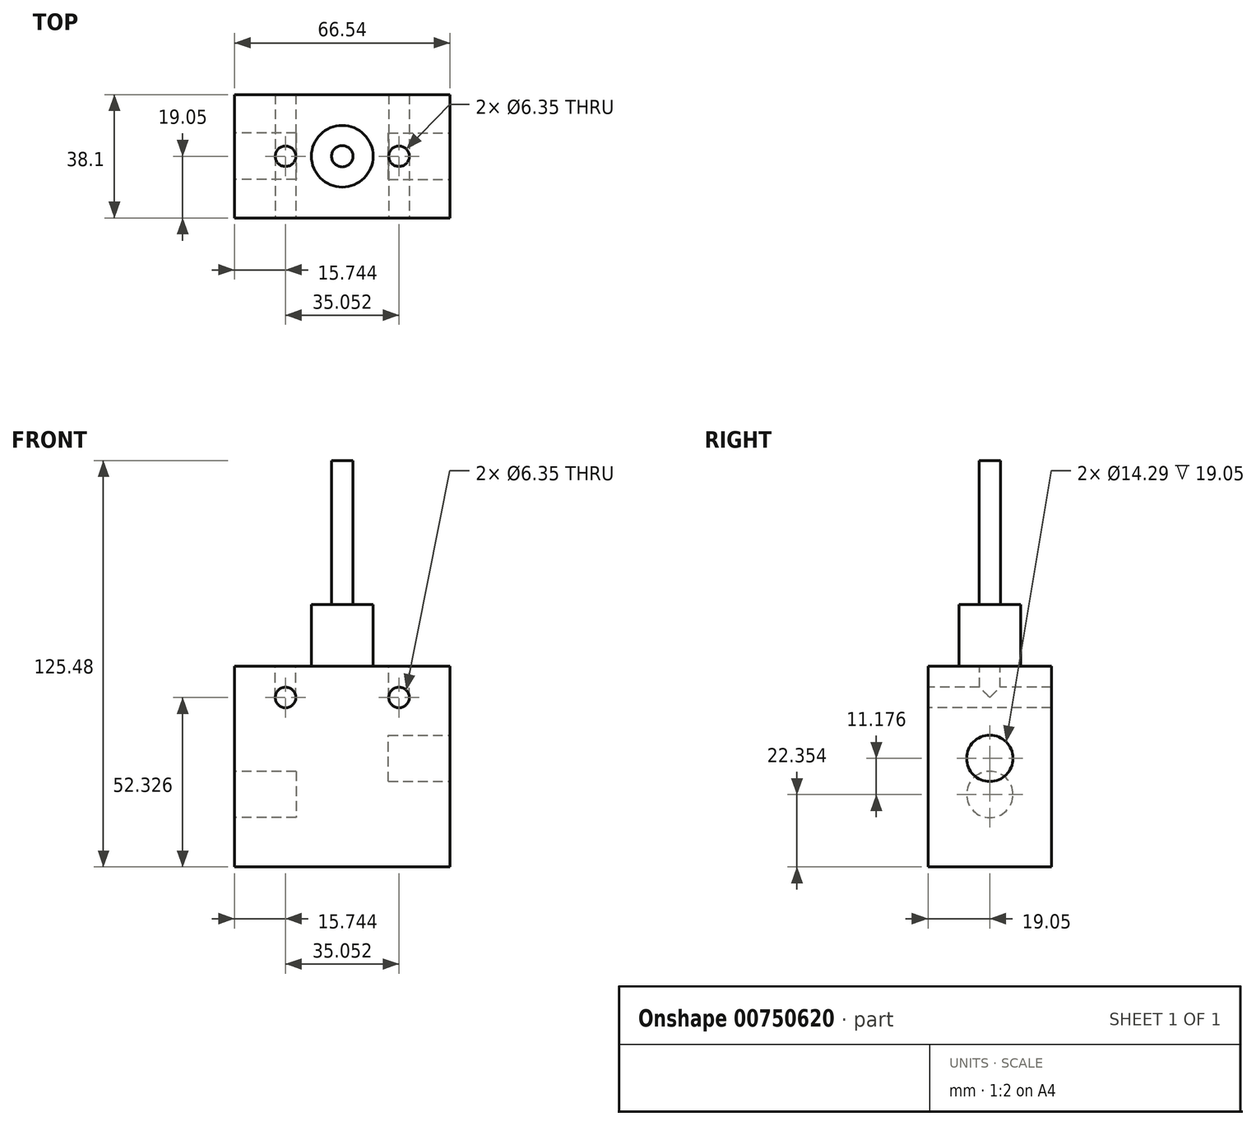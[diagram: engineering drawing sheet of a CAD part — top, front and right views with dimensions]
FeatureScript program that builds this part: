
annotation { "Feature Type Name" : "Feature", "Feature Type Description" : "" }
export const myFeature = defineFeature(function(context is Context, id is Id, definition is map)
    precondition{}
    {
        {
            var Q0;
            Q0=qCreatedBy(makeId("Front.planeOp"),FACE);
            var sketch = newSketch(context, id + "F0", { "sketchPlane" : qUnion([Q0])});
            skLineSegment(sketch, "E0.bottom", {"start": v(-33.27, 30.99) * mm, "end": v(33.27, 30.99) * mm});
            skLineSegment(sketch, "E0.top", {"start": v(-33.27, -30.99) * mm, "end": v(33.27, -30.99) * mm});
            skLineSegment(sketch, "E0.left", {"start": v(-33.27, 30.99) * mm, "end": v(-33.27, -30.99) * mm});
            skLineSegment(sketch, "E0.right", {"start": v(33.27, 30.99) * mm, "end": v(33.27, -30.99) * mm});
            skSolve(sketch);
        }
        {
            var Q0;
            Q0=makeQuery(id+"F0.imprint","IMPRINT",FACE,{"disambiguationData":[TD([[makeQuery(id+"F0.imprint","IMPRINT",EDGE,{"derivedFrom":sQuery(id+"F0.wireOp",EDGE,"E0.bottom")}),-1.0]])]});
            extrude(context, id + "F1", {"entities" : qUnion([Q0]), "endBound" : BoundingType.SYMMETRIC, "depth" : 38.1 * mm, "offsetDistance" : 25.4 * mm});
        }
        {
            var Q0;
            Q0=makeQuery(id+"F1.opExtrude","SWEPT_FACE",FACE,{"disambiguationData":[OSD([sQuery(id+"F0.wireOp",EDGE,"E0.bottom")])]});
            var sketch = newSketch(context, id + "F2", { "sketchPlane" : qUnion([Q0])});
            skCircle(sketch, "E1", {"center": v(0, 0) * mm, "radius": 9.53 * mm});
            skCircle(sketch, "E2", {"center": v(0, 0) * mm, "radius": 3.3 * mm});
            skCircle(sketch, "E3", {"center": v(-17.53, 0) * mm, "radius": 3.18 * mm});
            skCircle(sketch, "E4", {"center": v(17.53, 0) * mm, "radius": 3.18 * mm});
            skSolve(sketch);
        }
        {
            var Q0;
            Q0=makeQuery(id+"F2.imprint","IMPRINT",FACE,{"disambiguationData":[TD([[makeQuery(id+"F2.imprint","IMPRINT",EDGE,{"derivedFrom":sQuery(id+"F2.wireOp",EDGE,"E1")}),1.0]])]});
            extrude(context, id + "F3", {"entities" : qUnion([Q0]), "operationType" : NewBodyOperationType.ADD, "depth" : 19.05 * mm, "offsetDistance" : 25.4 * mm});
        }
        {
            var Q0;
            Q0=makeQuery(id+"F3.boolean.opBoolean","SPLIT",FACE,{"disambiguationData":[TD([makeQuery(id+"F3.opExtrude","SWEPT_FACE",FACE,{"disambiguationData":[OSD([sQuery(id+"F2.wireOp",EDGE,"E2")])]})])],"derivedFrom":makeQuery(id+"F1.opExtrude","SWEPT_FACE",FACE,{"disambiguationData":[OSD([sQuery(id+"F0.wireOp",EDGE,"E0.bottom")])]})});
            extrude(context, id + "F4", {"entities" : qUnion([Q0]), "operationType" : NewBodyOperationType.ADD, "depth" : 63.5 * mm, "offsetDistance" : 25.4 * mm});
        }
        {
            var Q0;
            Q0=makeQuery(id+"F2.imprint","IMPRINT",FACE,{"disambiguationData":[TD([[makeQuery(id+"F2.imprint","IMPRINT",EDGE,{"derivedFrom":sQuery(id+"F2.wireOp",EDGE,"E3")}),1.0]])]});
            var Q1;
            Q1=makeQuery(id+"F2.imprint","IMPRINT",FACE,{"disambiguationData":[TD([[makeQuery(id+"F2.imprint","IMPRINT",EDGE,{"derivedFrom":sQuery(id+"F2.wireOp",EDGE,"E4")}),1.0]])]});
            extrude(context, id + "F5", {"entities" : qUnion([Q0, Q1]), "operationType" : NewBodyOperationType.REMOVE, "oppositeDirection" : true, "depth" : 9.65 * mm, "offsetDistance" : 25.4 * mm});
        }
        {
            var Q0;
            Q0=makeQuery(id+"F1.opExtrude","CAP_FACE",FACE,{"disambiguationData":[OSD([sQuery(id+"F0.wireOp",EDGE,"E0.bottom"),sQuery(id+"F0.wireOp",EDGE,"E0.top"),sQuery(id+"F0.wireOp",EDGE,"E0.left"),sQuery(id+"F0.wireOp",EDGE,"E0.right")])],"isStart":false});
            var sketch = newSketch(context, id + "F6", { "sketchPlane" : qUnion([Q0])});
            skCircle(sketch, "E5", {"center": v(-17.53, 21.34) * mm, "radius": 3.18 * mm});
            skCircle(sketch, "E6", {"center": v(17.53, 21.34) * mm, "radius": 3.18 * mm});
            skSolve(sketch);
        }
        {
            var Q0;
            Q0=makeQuery(id+"F6.imprint","IMPRINT",FACE,{"disambiguationData":[TD([[makeQuery(id+"F6.imprint","IMPRINT",EDGE,{"derivedFrom":sQuery(id+"F6.wireOp",EDGE,"E5")}),1.0]])]});
            var Q1;
            Q1=makeQuery(id+"F6.imprint","IMPRINT",FACE,{"disambiguationData":[TD([[makeQuery(id+"F6.imprint","IMPRINT",EDGE,{"derivedFrom":sQuery(id+"F6.wireOp",EDGE,"E6")}),1.0]])]});
            extrude(context, id + "F7", {"entities" : qUnion([Q0, Q1]), "operationType" : NewBodyOperationType.REMOVE, "endBound" : BoundingType.THROUGH_ALL, "oppositeDirection" : true, "depth" : 25.4 * mm, "offsetDistance" : 25.4 * mm});
        }
        {
            var Q0;
            Q0=makeQuery(id+"F1.opExtrude","SWEPT_FACE",FACE,{"disambiguationData":[OSD([sQuery(id+"F0.wireOp",EDGE,"E0.right")])]});
            var sketch = newSketch(context, id + "F8", { "sketchPlane" : qUnion([Q0])});
            skCircle(sketch, "E7", {"center": v(0, 2.54) * mm, "radius": 7.14 * mm});
            skSolve(sketch);
        }
        {
            var Q0;
            Q0=makeQuery(id+"F8.imprint","IMPRINT",FACE,{"disambiguationData":[TD([[makeQuery(id+"F8.imprint","IMPRINT",EDGE,{"derivedFrom":sQuery(id+"F8.wireOp",EDGE,"E7")}),1.0]])]});
            extrude(context, id + "F9", {"entities" : qUnion([Q0]), "operationType" : NewBodyOperationType.REMOVE, "oppositeDirection" : true, "depth" : 19.05 * mm, "offsetDistance" : 25.4 * mm});
        }
        {
            var Q0;
            Q0=makeQuery(id+"F1.opExtrude","SWEPT_FACE",FACE,{"disambiguationData":[OSD([sQuery(id+"F0.wireOp",EDGE,"E0.left")])]});
            var sketch = newSketch(context, id + "F10", { "sketchPlane" : qUnion([Q0])});
            skCircle(sketch, "E8", {"center": v(0, -8.64) * mm, "radius": 7.14 * mm});
            skSolve(sketch);
        }
        {
            var Q0;
            Q0=makeQuery(id+"F10.imprint","IMPRINT",FACE,{"disambiguationData":[TD([[makeQuery(id+"F10.imprint","IMPRINT",EDGE,{"derivedFrom":sQuery(id+"F10.wireOp",EDGE,"E8")}),1.0]])]});
            extrude(context, id + "F11", {"entities" : qUnion([Q0]), "operationType" : NewBodyOperationType.REMOVE, "oppositeDirection" : true, "depth" : 19.05 * mm, "offsetDistance" : 25.4 * mm});
        }
    });
